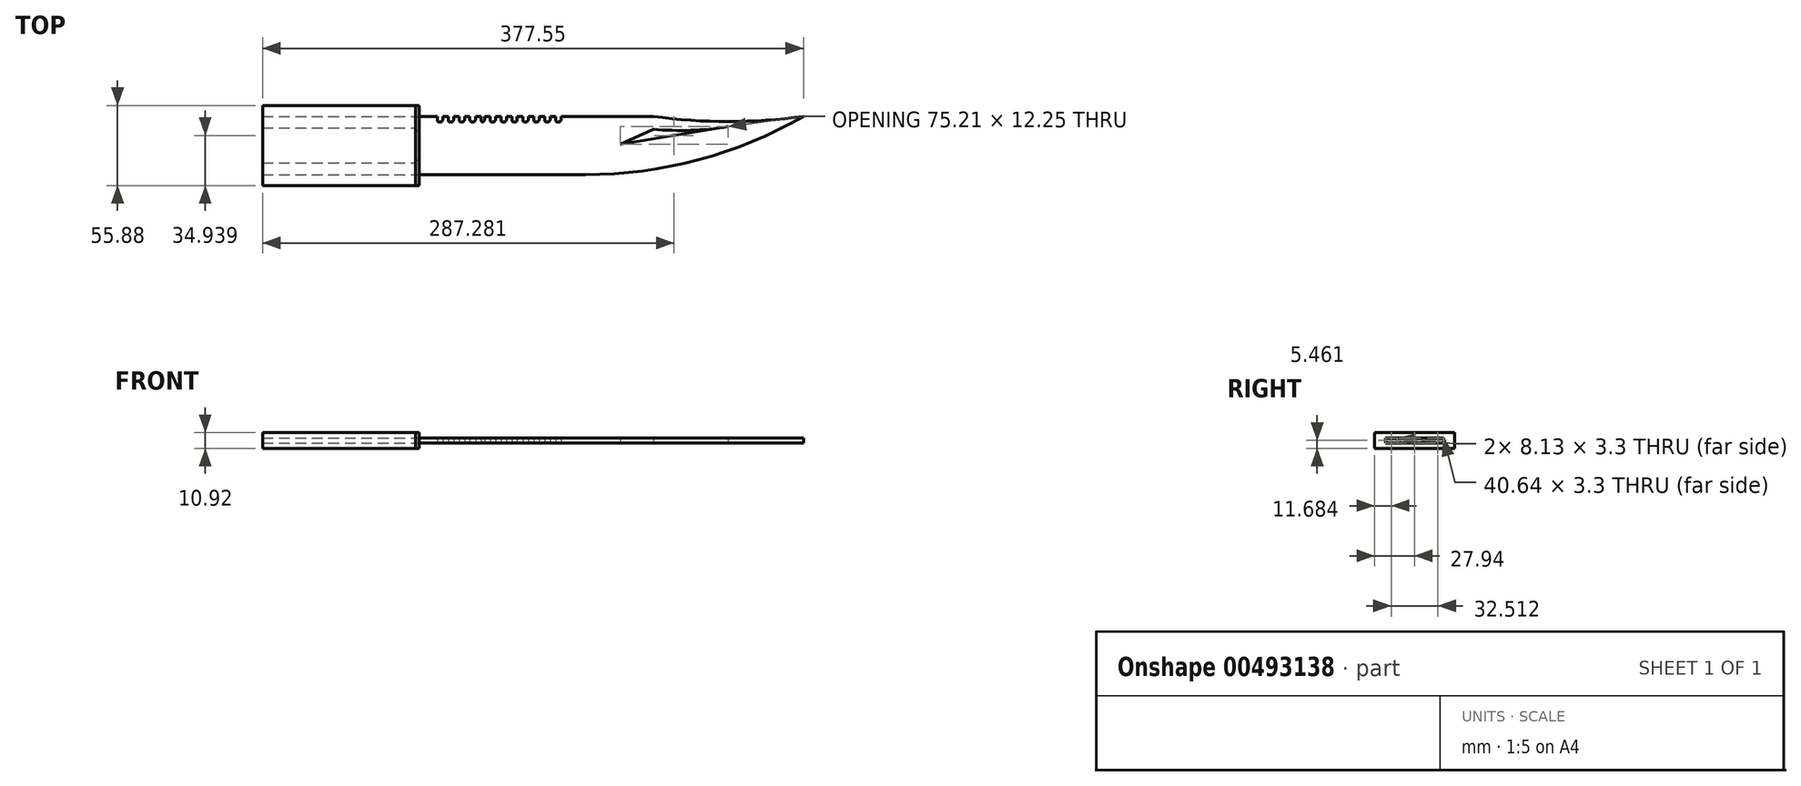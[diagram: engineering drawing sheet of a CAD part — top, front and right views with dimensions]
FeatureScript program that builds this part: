
annotation { "Feature Type Name" : "Feature", "Feature Type Description" : "" }
export const myFeature = defineFeature(function(context is Context, id is Id, definition is map)
    precondition{}
    {
        {
            var Q0;
            Q0=qCreatedBy(makeId("Top.planeOp"),FACE);
            var sketch = newSketch(context, id + "F0", { "sketchPlane" : qUnion([Q0])});
            skPoint(sketch, "E0", {"position": v(-2.63, 15.24) * mm});
            skPoint(sketch, "E1", {"position": v(-2.63, -45.72) * mm});
            skPoint(sketch, "E2.endSnap0", {"position": v(-0.1, -15.24) * mm});
            skLineSegment(sketch, "E3", {"start": v(2.45, -40.64) * mm, "end": v(118.72, -40.64) * mm});
            skPoint(sketch, "E4.end.orphan", {"position": v(231.58, -15.24) * mm});
            skPoint(sketch, "E5", {"position": v(270.78, 0) * mm});
            skArc(sketch, "E6", {"start": v(118.72, -40.64) * mm, "mid": v(197.42, -30.3) * mm, "end": v(270.78, 0) * mm});
            skArc(sketch, "E7", {"start": v(166.02, 0) * mm, "mid": v(218.4, -3.62) * mm, "end": v(270.78, 0) * mm});
            skLineSegment(sketch, "E8", {"start": v(2.45, 0) * mm, "end": v(15.15, 0) * mm});
            skArc(sketch, "E9", {"start": v(166.02, -8.9) * mm, "mid": v(192.12, -9.73) * mm, "end": v(218.12, -7.2) * mm});
            skLineSegment(sketch, "E10", {"start": v(218.12, -7.2) * mm, "end": v(142.9, -19.45) * mm});
            skLineSegment(sketch, "E11", {"start": v(166.02, -8.9) * mm, "end": v(142.9, -19.45) * mm});
            skLineSegment(sketch, "E12", {"start": v(15.15, 0) * mm, "end": v(15.15, -2.54) * mm});
            skLineSegment(sketch, "E13", {"start": v(16.42, -3.8) * mm, "end": v(17.69, -3.8) * mm});
            skLineSegment(sketch, "E14", {"start": v(18.96, -2.54) * mm, "end": v(18.96, 0) * mm});
            skLineSegment(sketch, "E15", {"start": v(22.77, 0) * mm, "end": v(22.77, -2.54) * mm});
            skLineSegment(sketch, "E16", {"start": v(24.04, -3.8) * mm, "end": v(25.3, -3.8) * mm});
            skLineSegment(sketch, "E17", {"start": v(26.58, -2.54) * mm, "end": v(26.58, 0) * mm});
            skLineSegment(sketch, "E18", {"start": v(30.39, 0) * mm, "end": v(30.39, -2.54) * mm});
            skLineSegment(sketch, "E19", {"start": v(31.66, -3.8) * mm, "end": v(32.93, -3.8) * mm});
            skLineSegment(sketch, "E20", {"start": v(34.2, -2.54) * mm, "end": v(34.2, 0) * mm});
            skLineSegment(sketch, "E21", {"start": v(38, 0) * mm, "end": v(38, -2.54) * mm});
            skLineSegment(sketch, "E22", {"start": v(39.28, -3.8) * mm, "end": v(40.55, -3.8) * mm});
            skLineSegment(sketch, "E23", {"start": v(41.82, -2.54) * mm, "end": v(41.82, 0) * mm});
            skLineSegment(sketch, "E24", {"start": v(45.63, 0) * mm, "end": v(45.63, -2.54) * mm});
            skLineSegment(sketch, "E25", {"start": v(46.9, -3.8) * mm, "end": v(46.9, -3.8) * mm});
            skLineSegment(sketch, "E26", {"start": v(48.17, -2.54) * mm, "end": v(48.17, 0) * mm});
            skLineSegment(sketch, "E27", {"start": v(51.98, 0) * mm, "end": v(51.98, -2.54) * mm});
            skLineSegment(sketch, "E28", {"start": v(53.25, -3.8) * mm, "end": v(54.52, -3.8) * mm});
            skLineSegment(sketch, "E29", {"start": v(55.79, -2.54) * mm, "end": v(55.79, 0) * mm});
            skLineSegment(sketch, "E30.trimOffspring", {"start": v(18.96, 0) * mm, "end": v(22.77, 0) * mm});
            skLineSegment(sketch, "E31.trimOffspring", {"start": v(26.58, 0) * mm, "end": v(30.39, 0) * mm});
            skLineSegment(sketch, "E32.trimOffspring", {"start": v(41.82, 0) * mm, "end": v(45.63, 0) * mm});
            skLineSegment(sketch, "E33", {"start": v(34.2, 0) * mm, "end": v(38, 0) * mm});
            skLineSegment(sketch, "E34.trimOffspring", {"start": v(55.79, 0) * mm, "end": v(59.6, 0) * mm});
            skLineSegment(sketch, "E35.trimOffspring", {"start": v(48.17, 0) * mm, "end": v(51.98, 0) * mm});
            skLineSegment(sketch, "E36", {"start": v(59.6, 0) * mm, "end": v(59.6, -2.54) * mm});
            skLineSegment(sketch, "E37", {"start": v(60.87, -3.8) * mm, "end": v(62.14, -3.8) * mm});
            skLineSegment(sketch, "E38", {"start": v(63.4, -2.54) * mm, "end": v(63.4, 0) * mm});
            skLineSegment(sketch, "E39", {"start": v(67.22, 0) * mm, "end": v(67.22, -2.54) * mm});
            skLineSegment(sketch, "E40", {"start": v(68.49, -3.8) * mm, "end": v(69.76, -3.8) * mm});
            skLineSegment(sketch, "E41", {"start": v(71.03, -2.54) * mm, "end": v(71.03, 0) * mm});
            skLineSegment(sketch, "E42.trimOffspring", {"start": v(63.4, 0) * mm, "end": v(67.22, 0) * mm});
            skLineSegment(sketch, "E43.trimOffspring", {"start": v(71.03, 0) * mm, "end": v(74.84, 0) * mm});
            skPoint(sketch, "E44.visualSharp", {"position": v(18.96, -3.8) * mm});
            skArc(sketch, "E44.filletArc", {"start": v(17.69, -3.8) * mm, "mid": v(18.59, -3.44) * mm, "end": v(18.96, -2.54) * mm});
            skPoint(sketch, "E45.visualSharp", {"position": v(15.15, -3.8) * mm});
            skArc(sketch, "E45.filletArc", {"start": v(15.15, -2.54) * mm, "mid": v(15.52, -3.44) * mm, "end": v(16.42, -3.8) * mm});
            skPoint(sketch, "E46.visualSharp", {"position": v(22.77, -3.8) * mm});
            skArc(sketch, "E46.filletArc", {"start": v(22.77, -2.54) * mm, "mid": v(23.14, -3.44) * mm, "end": v(24.04, -3.8) * mm});
            skPoint(sketch, "E47.visualSharp", {"position": v(26.58, -3.8) * mm});
            skArc(sketch, "E47.filletArc", {"start": v(25.3, -3.8) * mm, "mid": v(26.2, -3.44) * mm, "end": v(26.58, -2.54) * mm});
            skPoint(sketch, "E48.visualSharp", {"position": v(30.39, -3.8) * mm});
            skArc(sketch, "E48.filletArc", {"start": v(30.39, -2.54) * mm, "mid": v(30.76, -3.44) * mm, "end": v(31.66, -3.8) * mm});
            skPoint(sketch, "E49.visualSharp", {"position": v(34.2, -3.8) * mm});
            skArc(sketch, "E49.filletArc", {"start": v(32.93, -3.8) * mm, "mid": v(33.83, -3.44) * mm, "end": v(34.2, -2.54) * mm});
            skPoint(sketch, "E50.visualSharp", {"position": v(38, -3.8) * mm});
            skArc(sketch, "E50.filletArc", {"start": v(38, -2.54) * mm, "mid": v(38.38, -3.44) * mm, "end": v(39.28, -3.8) * mm});
            skPoint(sketch, "E51.visualSharp", {"position": v(41.82, -3.8) * mm});
            skArc(sketch, "E51.filletArc", {"start": v(40.55, -3.8) * mm, "mid": v(41.45, -3.44) * mm, "end": v(41.82, -2.54) * mm});
            skPoint(sketch, "E52.visualSharp", {"position": v(45.63, -3.8) * mm});
            skArc(sketch, "E52.filletArc", {"start": v(45.63, -2.54) * mm, "mid": v(46, -3.44) * mm, "end": v(46.9, -3.8) * mm});
            skPoint(sketch, "E53.visualSharp", {"position": v(48.17, -3.8) * mm});
            skArc(sketch, "E53.filletArc", {"start": v(46.9, -3.8) * mm, "mid": v(47.8, -3.44) * mm, "end": v(48.17, -2.54) * mm});
            skPoint(sketch, "E54.visualSharp", {"position": v(51.98, -3.8) * mm});
            skArc(sketch, "E54.filletArc", {"start": v(51.98, -2.54) * mm, "mid": v(52.35, -3.44) * mm, "end": v(53.25, -3.8) * mm});
            skPoint(sketch, "E55.visualSharp", {"position": v(55.79, -3.8) * mm});
            skArc(sketch, "E55.filletArc", {"start": v(54.52, -3.8) * mm, "mid": v(55.42, -3.44) * mm, "end": v(55.79, -2.54) * mm});
            skPoint(sketch, "E56.visualSharp", {"position": v(59.6, -3.8) * mm});
            skArc(sketch, "E56.filletArc", {"start": v(59.6, -2.54) * mm, "mid": v(59.97, -3.44) * mm, "end": v(60.87, -3.8) * mm});
            skPoint(sketch, "E57.visualSharp", {"position": v(63.4, -3.8) * mm});
            skArc(sketch, "E57.filletArc", {"start": v(62.14, -3.8) * mm, "mid": v(63.04, -3.44) * mm, "end": v(63.4, -2.54) * mm});
            skPoint(sketch, "E58.visualSharp", {"position": v(67.22, -3.8) * mm});
            skArc(sketch, "E58.filletArc", {"start": v(67.22, -2.54) * mm, "mid": v(67.6, -3.44) * mm, "end": v(68.49, -3.8) * mm});
            skPoint(sketch, "E59.visualSharp", {"position": v(71.03, -3.8) * mm});
            skArc(sketch, "E59.filletArc", {"start": v(69.76, -3.8) * mm, "mid": v(70.66, -3.44) * mm, "end": v(71.03, -2.54) * mm});
            skLineSegment(sketch, "E60", {"start": v(74.84, 0) * mm, "end": v(74.84, -2.54) * mm});
            skLineSegment(sketch, "E61", {"start": v(76.1, -3.8) * mm, "end": v(77.38, -3.8) * mm});
            skLineSegment(sketch, "E62", {"start": v(78.65, -2.54) * mm, "end": v(78.65, 0) * mm});
            skLineSegment(sketch, "E63", {"start": v(82.46, 0) * mm, "end": v(82.46, -2.54) * mm});
            skLineSegment(sketch, "E64", {"start": v(83.73, -3.8) * mm, "end": v(85, -3.8) * mm});
            skLineSegment(sketch, "E65", {"start": v(86.27, -2.54) * mm, "end": v(86.27, 0) * mm});
            skLineSegment(sketch, "E66", {"start": v(90.08, 0) * mm, "end": v(90.08, -2.54) * mm});
            skLineSegment(sketch, "E67", {"start": v(91.35, -3.8) * mm, "end": v(92.62, -3.8) * mm});
            skLineSegment(sketch, "E68", {"start": v(93.89, -2.54) * mm, "end": v(93.89, 0) * mm});
            skLineSegment(sketch, "E69", {"start": v(97.7, 0) * mm, "end": v(97.7, -2.54) * mm});
            skLineSegment(sketch, "E70", {"start": v(98.97, -3.8) * mm, "end": v(100.24, -3.8) * mm});
            skLineSegment(sketch, "E71", {"start": v(101.5, -2.54) * mm, "end": v(101.5, 0) * mm});
            skPoint(sketch, "E72.visualSharp", {"position": v(74.84, -3.8) * mm});
            skArc(sketch, "E72.filletArc", {"start": v(74.84, -2.54) * mm, "mid": v(75.21, -3.44) * mm, "end": v(76.1, -3.8) * mm});
            skPoint(sketch, "E73.visualSharp", {"position": v(78.65, -3.8) * mm});
            skArc(sketch, "E73.filletArc", {"start": v(77.38, -3.8) * mm, "mid": v(78.28, -3.44) * mm, "end": v(78.65, -2.54) * mm});
            skPoint(sketch, "E74.visualSharp", {"position": v(82.46, -3.8) * mm});
            skArc(sketch, "E74.filletArc", {"start": v(82.46, -2.54) * mm, "mid": v(82.83, -3.44) * mm, "end": v(83.73, -3.8) * mm});
            skPoint(sketch, "E75.visualSharp", {"position": v(86.27, -3.8) * mm});
            skArc(sketch, "E75.filletArc", {"start": v(85, -3.81) * mm, "mid": v(85.9, -3.44) * mm, "end": v(86.27, -2.54) * mm});
            skPoint(sketch, "E76.visualSharp", {"position": v(90.08, -3.81) * mm});
            skArc(sketch, "E76.filletArc", {"start": v(90.08, -2.54) * mm, "mid": v(90.45, -3.44) * mm, "end": v(91.35, -3.8) * mm});
            skPoint(sketch, "E77.visualSharp", {"position": v(93.89, -3.81) * mm});
            skArc(sketch, "E77.filletArc", {"start": v(92.62, -3.8) * mm, "mid": v(93.52, -3.44) * mm, "end": v(93.89, -2.54) * mm});
            skPoint(sketch, "E78.visualSharp", {"position": v(97.7, -3.81) * mm});
            skArc(sketch, "E78.filletArc", {"start": v(97.7, -2.54) * mm, "mid": v(98.07, -3.44) * mm, "end": v(98.97, -3.8) * mm});
            skPoint(sketch, "E79.visualSharp", {"position": v(101.5, -3.81) * mm});
            skArc(sketch, "E79.filletArc", {"start": v(100.24, -3.8) * mm, "mid": v(101.14, -3.44) * mm, "end": v(101.5, -2.54) * mm});
            skLineSegment(sketch, "E80.trimOffspring", {"start": v(78.65, 0) * mm, "end": v(82.46, 0) * mm});
            skLineSegment(sketch, "E81.trimOffspring", {"start": v(86.27, 0) * mm, "end": v(90.08, 0) * mm});
            skLineSegment(sketch, "E82.trimOffspring", {"start": v(93.89, 0) * mm, "end": v(97.7, 0) * mm});
            skLineSegment(sketch, "E83.trimOffspring", {"start": v(101.5, 0) * mm, "end": v(166.02, 0) * mm});
            skPoint(sketch, "E84.end.orphan", {"position": v(-93.77, -25.4) * mm});
            skPoint(sketch, "E84.start.orphan", {"position": v(-93.77, 0) * mm});
            skPoint(sketch, "E85.orphan", {"position": v(0.91, -40.64) * mm});
            skLineSegment(sketch, "E86", {"start": v(2.45, -40.64) * mm, "end": v(2.45, -30.48) * mm});
            skLineSegment(sketch, "E87", {"start": v(2.45, 0) * mm, "end": v(2.45, -10.16) * mm});
            skLineSegment(sketch, "E88", {"start": v(2.45, -10.16) * mm, "end": v(-99.15, -10.16) * mm});
            skLineSegment(sketch, "E89", {"start": v(-99.15, -10.16) * mm, "end": v(-99.15, -30.48) * mm});
            skLineSegment(sketch, "E90", {"start": v(-99.15, -30.48) * mm, "end": v(2.45, -30.48) * mm});
            skPoint(sketch, "E91.orphan", {"position": v(-93.77, -7.62) * mm});
            skPoint(sketch, "E92.end.orphan", {"position": v(-93.77, -27.94) * mm});
            skSolve(sketch);
        }
        {
            var Q0;
            Q0=makeQuery(id+"F0.imprint","IMPRINT",FACE,{"disambiguationData":[TD([[makeQuery(id+"F0.imprint","IMPRINT",EDGE,{"derivedFrom":sQuery(id+"F0.wireOp",EDGE,"E3")}),1.0]])]});
            extrude(context, id + "F1", {"entities" : qUnion([Q0]), "depth" : 3.3 * mm});
        }
        {
            var Q0;
            Q0=makeQuery(id+"F1.opExtrude","SWEPT_FACE",FACE,{"disambiguationData":[OSD([sQuery(id+"F0.wireOp",EDGE,"E86")])]});
            var sketch = newSketch(context, id + "F2", { "sketchPlane" : qUnion([Q0])});
            skLineSegment(sketch, "E93", {"start": v(35.56, 7.11) * mm, "end": v(0, 7.11) * mm});
            skLineSegment(sketch, "E94", {"start": v(5.08, -3.81) * mm, "end": v(40.64, -3.81) * mm});
            skLineSegment(sketch, "E95", {"start": v(40.64, -3.81) * mm, "end": v(48.26, -3.81) * mm});
            skLineSegment(sketch, "E96", {"start": v(48.26, -3.81) * mm, "end": v(48.26, 7.11) * mm});
            skLineSegment(sketch, "E97", {"start": v(48.26, 7.11) * mm, "end": v(35.56, 7.11) * mm});
            skLineSegment(sketch, "E98", {"start": v(5.08, -3.81) * mm, "end": v(-7.62, -3.81) * mm});
            skLineSegment(sketch, "E99", {"start": v(-7.62, -3.81) * mm, "end": v(-7.62, 7.11) * mm});
            skLineSegment(sketch, "E100", {"start": v(-7.62, 7.11) * mm, "end": v(0, 7.11) * mm});
            skLineSegment(sketch, "E101.0", {"start": v(2.54, 0) * mm, "end": v(27.94, 0) * mm});
            skLineSegment(sketch, "E102.0", {"start": v(33.02, 0) * mm, "end": v(40.64, 0) * mm});
            skLineSegment(sketch, "E103.0", {"start": v(40.64, 3.3) * mm, "end": v(40.64, 0) * mm});
            skLineSegment(sketch, "E104.0", {"start": v(33.02, 3.3) * mm, "end": v(40.64, 3.3) * mm});
            skLineSegment(sketch, "E105.0", {"start": v(2.54, 3.3) * mm, "end": v(27.94, 3.3) * mm});
            skLineSegment(sketch, "E106.0", {"start": v(2.54, 3.3) * mm, "end": v(0, 3.3) * mm});
            skLineSegment(sketch, "E107.0", {"start": v(0, 3.3) * mm, "end": v(0, 0) * mm});
            skLineSegment(sketch, "E108", {"start": v(0, 0) * mm, "end": v(2.54, 0) * mm});
            skLineSegment(sketch, "E109", {"start": v(0, 0) * mm, "end": v(40.64, 0) * mm});
            skLineSegment(sketch, "E110", {"start": v(40.64, 3.3) * mm, "end": v(0, 3.3) * mm});
            skSolve(sketch);
        }
        {
            var Q0;
            Q0=makeQuery(id+"F2.imprint","IMPRINT",FACE,{"disambiguationData":[TD([[makeQuery(id+"F2.imprint","IMPRINT",EDGE,{"derivedFrom":sQuery(id+"F2.wireOp",EDGE,"E93")}),1.0]])]});
            extrude(context, id + "F3", {"entities" : qUnion([Q0]), "depth" : 2.54 * mm});
        }
        {
            var Q0;
            Q0=makeQuery(id+"F3.opExtrude","CAP_FACE",FACE,{"disambiguationData":[OSD([sQuery(id+"F2.wireOp",EDGE,"E93"),sQuery(id+"F2.wireOp",EDGE,"E94"),sQuery(id+"F2.wireOp",EDGE,"E95"),sQuery(id+"F2.wireOp",EDGE,"E96"),sQuery(id+"F2.wireOp",EDGE,"E97"),sQuery(id+"F2.wireOp",EDGE,"E98"),sQuery(id+"F2.wireOp",EDGE,"E99"),sQuery(id+"F2.wireOp",EDGE,"E100"),sQuery(id+"F2.wireOp",EDGE,"E107.0"),sQuery(id+"F2.wireOp",EDGE,"E109"),sQuery(id+"F2.wireOp",EDGE,"E103.0"),sQuery(id+"F2.wireOp",EDGE,"E110")])],"isStart":false});
            var sketch = newSketch(context, id + "F4", { "sketchPlane" : qUnion([Q0])});
            skLineSegment(sketch, "E111.0", {"start": v(10.16, 0) * mm, "end": v(30.48, 0) * mm});
            skLineSegment(sketch, "E112.0", {"start": v(30.48, 3.3) * mm, "end": v(30.48, 0) * mm});
            skLineSegment(sketch, "E113.0", {"start": v(10.16, 3.3) * mm, "end": v(30.48, 3.3) * mm});
            skLineSegment(sketch, "E114.0", {"start": v(10.16, 3.3) * mm, "end": v(10.16, 0) * mm});
            skLineSegment(sketch, "E115.1", {"start": v(8.13, 3.3) * mm, "end": v(8.13, 0) * mm});
            skLineSegment(sketch, "E115.3", {"start": v(32.51, 0) * mm, "end": v(32.51, 3.3) * mm});
            skPoint(sketch, "E116.visualSharp", {"position": v(8.13, 9.65) * mm});
            skArc(sketch, "E116.filletArc", {"start": v(10.16, 5.33) * mm, "mid": v(8.72, 4.74) * mm, "end": v(8.13, 3.3) * mm});
            skPoint(sketch, "E117.visualSharp", {"position": v(8.13, -6.35) * mm});
            skArc(sketch, "E117.filletArc", {"start": v(8.13, 0) * mm, "mid": v(8.72, -1.44) * mm, "end": v(10.16, -2.03) * mm});
            skPoint(sketch, "E118.visualSharp", {"position": v(32.51, -6.35) * mm});
            skArc(sketch, "E118.filletArc", {"start": v(30.48, -2.03) * mm, "mid": v(31.92, -1.44) * mm, "end": v(32.51, 0) * mm});
            skPoint(sketch, "E119.visualSharp", {"position": v(32.51, 9.65) * mm});
            skArc(sketch, "E119.filletArc", {"start": v(32.51, 3.3) * mm, "mid": v(31.92, 4.74) * mm, "end": v(30.48, 5.33) * mm});
            skArc(sketch, "E120", {"start": v(30.48, -2.03) * mm, "mid": v(20.32, -1.35) * mm, "end": v(10.16, -2.03) * mm});
            skLineSegment(sketch, "E121", {"start": v(10.16, 1.65) * mm, "end": v(30.48, 1.65) * mm, "construction": true});
            skArc(sketch, "E122.MirrorCS", {"start": v(30.48, 5.33) * mm, "mid": v(20.32, 4.65) * mm, "end": v(10.16, 5.33) * mm});
            skPoint(sketch, "E123.orphan", {"position": v(8.13, 1.65) * mm});
            skPoint(sketch, "E124.orphan", {"position": v(32.51, 1.65) * mm});
            skLineSegment(sketch, "E125", {"start": v(32.51, 3.3) * mm, "end": v(38.5, 3.3) * mm});
            skLineSegment(sketch, "E126", {"start": v(38.5, 3.3) * mm, "end": v(38.5, 0) * mm});
            skLineSegment(sketch, "E127", {"start": v(38.5, 0) * mm, "end": v(32.51, 0) * mm});
            skSolve(sketch);
        }
        {
            var Q0;
            {var subQ0=sQuery(id+"F4.wireOp",EDGE,"E114.0");Q0=makeQuery(id+"F4.imprint","IMPRINT",FACE,{"disambiguationData":[TD([[makeQuery(id+"F4.imprint","IMPRINT",EDGE,{"derivedFrom":subQ0}),-1.0]])]});}
            var Q1;
            {var subQ5=sQuery(id+"F4.wireOp",EDGE,"E113.0");Q1=makeQuery(id+"F4.imprint","IMPRINT",FACE,{"disambiguationData":[TD([[makeQuery(id+"F4.imprint","IMPRINT",EDGE,{"derivedFrom":subQ5}),-1.0]])]});}
            var Q2;
            {var subQ0=sQuery(id+"F4.wireOp",EDGE,"E112.0");Q2=makeQuery(id+"F4.imprint","IMPRINT",FACE,{"disambiguationData":[TD([[makeQuery(id+"F4.imprint","IMPRINT",EDGE,{"derivedFrom":subQ0}),1.0]])]});}
            var Q3;
            {var subQ5=sQuery(id+"F4.wireOp",EDGE,"E111.0");Q3=makeQuery(id+"F4.imprint","IMPRINT",FACE,{"disambiguationData":[TD([[makeQuery(id+"F4.imprint","IMPRINT",EDGE,{"derivedFrom":subQ5}),-1.0]])]});}
            var Q4;
            {var subQ0=sQuery(id+"F4.wireOp",EDGE,"E122.MirrorCS");Q4=makeQuery(id+"F4.imprint","IMPRINT",FACE,{"disambiguationData":[TD([[makeQuery(id+"F4.imprint","IMPRINT",EDGE,{"derivedFrom":subQ0}),1.0]])]});}
            var Q5;
            {var subQ0=sQuery(id+"F4.wireOp",EDGE,"E120");Q5=makeQuery(id+"F4.imprint","IMPRINT",FACE,{"disambiguationData":[TD([[makeQuery(id+"F4.imprint","IMPRINT",EDGE,{"derivedFrom":subQ0}),-1.0]])]});}
            extrude(context, id + "F5", {"entities" : qUnion([Q0, Q1, Q2, Q3, Q4, Q5]), "depth" : 106.68 * mm});
        }
        {
            var Q0;
            Q0=makeQuery(id+"F1.opExtrude","SWEPT_FACE",FACE,{"disambiguationData":[OSD([sQuery(id+"F0.wireOp",EDGE,"E89")])]});
            extrude(context, id + "F6", {"entities" : qUnion([Q0]), "operationType" : NewBodyOperationType.ADD, "depth" : 7.62 * mm});
        }
        {
            var Q0;
            Q0=makeQuery(id+"F6.boolean.opBoolean","MERGE",FACE,{"derivedFrom":[makeQuery(id+"F5.opExtrude","CAP_FACE",FACE,{"disambiguationData":[OSD([sQuery(id+"F4.wireOp",EDGE,"E111.0"),sQuery(id+"F4.wireOp",EDGE,"E112.0"),sQuery(id+"F4.wireOp",EDGE,"E113.0"),sQuery(id+"F4.wireOp",EDGE,"E114.0"),sQuery(id+"F4.wireOp",EDGE,"E115.1"),sQuery(id+"F4.wireOp",EDGE,"E115.3"),sQuery(id+"F4.wireOp",EDGE,"E116.filletArc"),sQuery(id+"F4.wireOp",EDGE,"E117.filletArc"),sQuery(id+"F4.wireOp",EDGE,"E118.filletArc"),sQuery(id+"F4.wireOp",EDGE,"E119.filletArc"),sQuery(id+"F4.wireOp",EDGE,"E120"),sQuery(id+"F4.wireOp",EDGE,"E122.MirrorCS")])],"isStart":false}),makeQuery(id+"F6.opExtrude","CAP_FACE",FACE,{"disambiguationData":[OSD([sQuery(id+"F0.wireOp",EDGE,"E89")])],"isStart":false})]});
            var sketch = newSketch(context, id + "F7", { "sketchPlane" : qUnion([Q0])});
            skArc(sketch, "E128.0", {"start": v(30.48, -2.03) * mm, "mid": v(20.32, -1.35) * mm, "end": v(10.16, -2.03) * mm});
            skArc(sketch, "E129.0", {"start": v(30.48, 5.33) * mm, "mid": v(20.32, 4.65) * mm, "end": v(10.16, 5.33) * mm});
            skArc(sketch, "E130", {"start": v(10.16, -2.03) * mm, "mid": v(20.32, -2.71) * mm, "end": v(30.48, -2.03) * mm});
            skArc(sketch, "E131", {"start": v(30.48, 5.33) * mm, "mid": v(20.32, 6.01) * mm, "end": v(10.16, 5.33) * mm});
            skSolve(sketch);
        }
        {
            var Q0;
            Q0=makeQuery(id+"F7.imprint","IMPRINT",FACE,{"disambiguationData":[TD([[makeQuery(id+"F7.imprint","IMPRINT",EDGE,{"derivedFrom":sQuery(id+"F7.wireOp",EDGE,"E128.0")}),1.0]])]});
            var Q1;
            Q1=makeQuery(id+"F7.imprint","IMPRINT",FACE,{"disambiguationData":[TD([[makeQuery(id+"F7.imprint","IMPRINT",EDGE,{"derivedFrom":sQuery(id+"F7.wireOp",EDGE,"E129.0")}),-1.0]])]});
            extrude(context, id + "F8", {"entities" : qUnion([Q0, Q1]), "operationType" : NewBodyOperationType.ADD, "oppositeDirection" : true, "depth" : 105.66 * mm, "offsetDistance" : 25.4 * mm});
        }
    });
